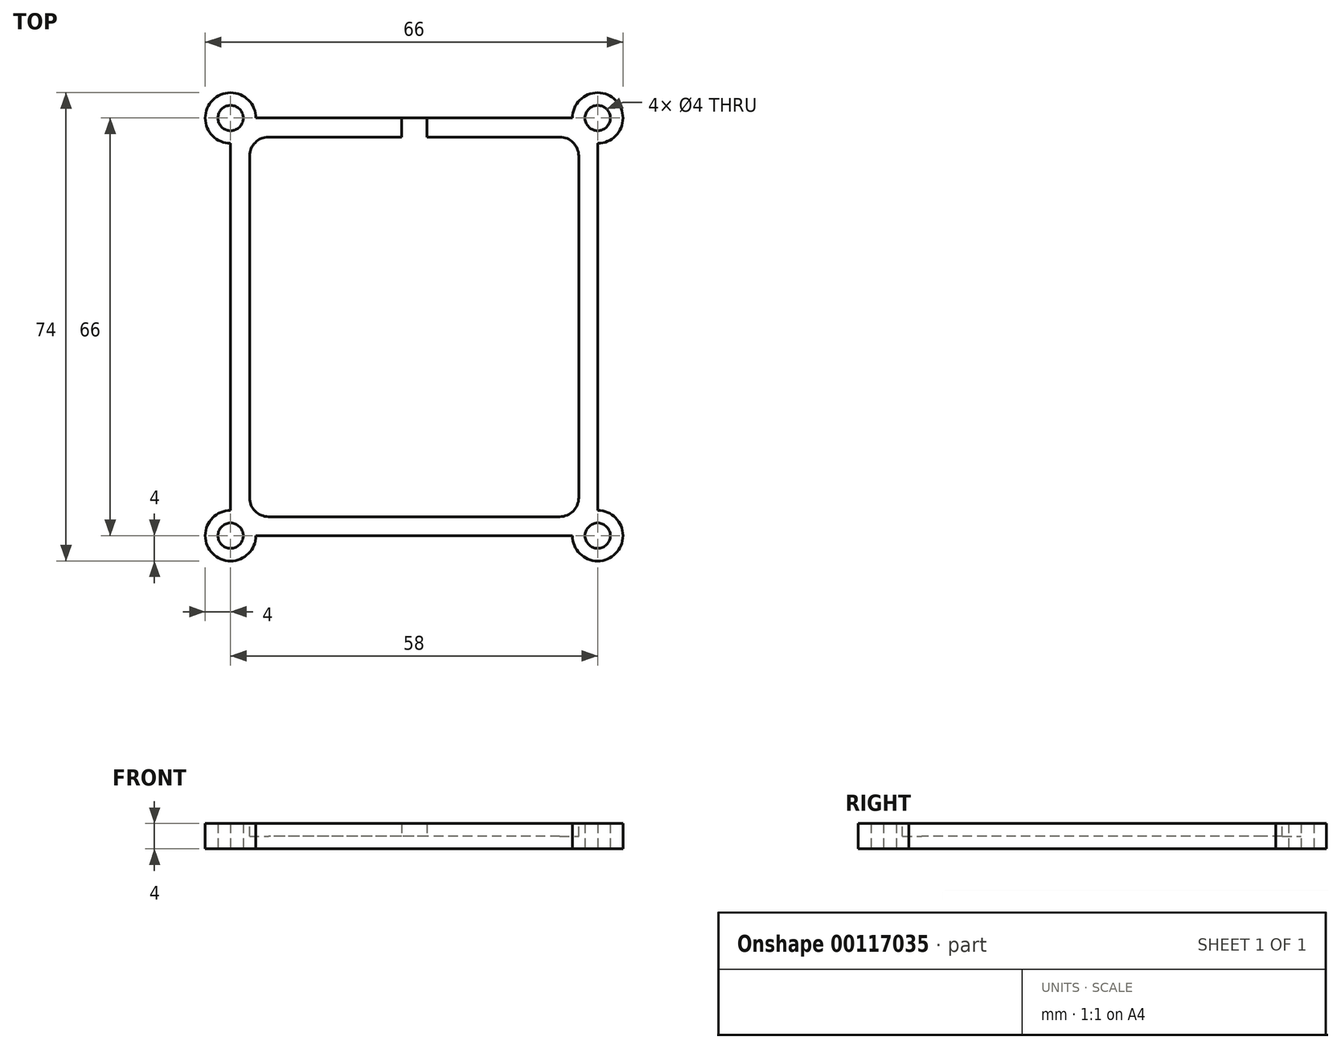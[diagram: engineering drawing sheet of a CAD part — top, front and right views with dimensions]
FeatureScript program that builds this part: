
annotation { "Feature Type Name" : "Feature", "Feature Type Description" : "" }
export const myFeature = defineFeature(function(context is Context, id is Id, definition is map)
    precondition{}
    {
        {
            var Q0;
            Q0=qCreatedBy(makeId("Top.planeOp"),FACE);
            var sketch = newSketch(context, id + "F0", { "sketchPlane" : qUnion([Q0])});
            skLineSegment(sketch, "E0.bottom", {"start": v(25, 29) * mm, "end": v(-25, 29) * mm, "construction": true});
            skLineSegment(sketch, "E0.top", {"start": v(25, -29) * mm, "end": v(-25, -29) * mm, "construction": true});
            skLineSegment(sketch, "E0.left", {"start": v(25, 29) * mm, "end": v(25, -29) * mm, "construction": true});
            skLineSegment(sketch, "E0.right", {"start": v(-25, 29) * mm, "end": v(-25, -29) * mm, "construction": true});
            skPoint(sketch, "E0.middle", {"position": v(0, 0) * mm});
            skLineSegment(sketch, "E1.bottom", {"start": v(-2, 33) * mm, "end": v(2, 33) * mm, "construction": true});
            skLineSegment(sketch, "E1.top", {"start": v(-2, 29) * mm, "end": v(2, 29) * mm, "construction": true});
            skLineSegment(sketch, "E1.left", {"start": v(-2, 33) * mm, "end": v(-2, 29) * mm, "construction": true});
            skLineSegment(sketch, "E1.right", {"start": v(2, 33) * mm, "end": v(2, 29) * mm, "construction": true});
            skPoint(sketch, "E2", {"position": v(0, 33) * mm});
            skSolve(sketch);
        }
        {
            var Q0;
            Q0=qCreatedBy(makeId("Top.planeOp"),FACE);
            var sketch = newSketch(context, id + "F1", { "sketchPlane" : qUnion([Q0])});
            skLineSegment(sketch, "E3.bottom", {"start": v(29, 33) * mm, "end": v(-29, 33) * mm});
            skLineSegment(sketch, "E3.top", {"start": v(29, -33) * mm, "end": v(-29, -33) * mm});
            skLineSegment(sketch, "E3.left", {"start": v(29, 33) * mm, "end": v(29, -33) * mm});
            skLineSegment(sketch, "E3.right", {"start": v(-29, 33) * mm, "end": v(-29, -33) * mm});
            skPoint(sketch, "E3.middle", {"position": v(0, 0) * mm});
            skCircle(sketch, "E4", {"center": v(29, 33) * mm, "radius": 4 * mm});
            skCircle(sketch, "E5.0.1.0", {"center": v(29, -33) * mm, "radius": 4 * mm});
            skCircle(sketch, "E5.1.0.0", {"center": v(-29, 33) * mm, "radius": 4 * mm});
            skCircle(sketch, "E5.1.1.0", {"center": v(-29, -33) * mm, "radius": 4 * mm});
            skLineSegment(sketch, "E5.direction1", {"start": v(29, 33) * mm, "end": v(-29, 33) * mm, "construction": true});
            skLineSegment(sketch, "E5.direction2", {"start": v(29, 33) * mm, "end": v(29, -33) * mm, "construction": true});
            skSolve(sketch);
        }
        {
            var Q0;
            Q0 = qSketchRegion(id + "F1", true);
            extrude(context, id + "F2", {"entities" : qUnion([Q0]), "depth" : 4 * mm});
        }
        {
            var Q0;
            Q0=makeQuery(id+"F2.opExtrude","SWEPT_FACE",FACE,{"disambiguationData":[OSD([sQuery(id+"F1.wireOp",EDGE,"E3.bottom")])]});
            var sketch = newSketch(context, id + "F3", { "sketchPlane" : qUnion([Q0])});
            skLineSegment(sketch, "E6.bottom", {"start": v(-2, 4) * mm, "end": v(2, 4) * mm});
            skLineSegment(sketch, "E6.top", {"start": v(-2, 2) * mm, "end": v(2, 2) * mm});
            skLineSegment(sketch, "E6.left", {"start": v(-2, 4) * mm, "end": v(-2, 2) * mm});
            skLineSegment(sketch, "E6.right", {"start": v(2, 4) * mm, "end": v(2, 2) * mm});
            skPoint(sketch, "E7", {"position": v(0, 4) * mm});
            skSolve(sketch);
        }
        {
            var Q0;
            Q0=makeQuery(id+"F3.imprint","IMPRINT",FACE,{"disambiguationData":[TD([[makeQuery(id+"F3.imprint","IMPRINT",EDGE,{"derivedFrom":sQuery(id+"F3.wireOp",EDGE,"E6.bottom")}),-1.0]])]});
            extrude(context, id + "F4", {"entities" : qUnion([Q0]), "operationType" : NewBodyOperationType.REMOVE, "oppositeDirection" : true, "depth" : 4 * mm});
        }
        {
            var Q0;
            Q0=makeQuery(id+"F2.opExtrude","CAP_FACE",FACE,{"disambiguationData":[OSD([sQuery(id+"F1.wireOp",EDGE,"E3.bottom"),sQuery(id+"F1.wireOp",EDGE,"E3.top"),sQuery(id+"F1.wireOp",EDGE,"E3.left"),sQuery(id+"F1.wireOp",EDGE,"E3.right"),sQuery(id+"F1.wireOp",EDGE,"E4"),sQuery(id+"F1.wireOp",EDGE,"E5.0.1.0"),sQuery(id+"F1.wireOp",EDGE,"E5.1.0.0"),sQuery(id+"F1.wireOp",EDGE,"E5.1.1.0")])],"isStart":false});
            var sketch = newSketch(context, id + "F5", { "sketchPlane" : qUnion([Q0])});
            skLineSegment(sketch, "E8.bottom", {"start": v(26, 30) * mm, "end": v(-26, 30) * mm});
            skLineSegment(sketch, "E8.top", {"start": v(26, -30) * mm, "end": v(-26, -30) * mm});
            skLineSegment(sketch, "E8.left", {"start": v(26, 30) * mm, "end": v(26, -30) * mm});
            skLineSegment(sketch, "E8.right", {"start": v(-26, 30) * mm, "end": v(-26, -30) * mm});
            skPoint(sketch, "E8.middle", {"position": v(0, 0) * mm});
            skSolve(sketch);
        }
        {
            var Q0;
            Q0 = qSketchRegion(id + "F5", true);
            extrude(context, id + "F6", {"entities" : qUnion([Q0]), "operationType" : NewBodyOperationType.REMOVE, "oppositeDirection" : true, "depth" : 2 * mm});
        }
        {
            var Q0;
            Q0=qCreatedBy(makeId("Top.planeOp"),FACE);
            var sketch = newSketch(context, id + "F7", { "sketchPlane" : qUnion([Q0])});
            skCircle(sketch, "E9", {"center": v(29, 33) * mm, "radius": 2 * mm});
            skCircle(sketch, "E10", {"center": v(-29, 33) * mm, "radius": 2 * mm});
            skCircle(sketch, "E11", {"center": v(29, -33) * mm, "radius": 2 * mm});
            skCircle(sketch, "E12", {"center": v(-29, -33) * mm, "radius": 2 * mm});
            skSolve(sketch);
        }
        {
            var Q0;
            Q0 = qSketchRegion(id + "F7", true);
            extrude(context, id + "F8", {"entities" : qUnion([Q0]), "operationType" : NewBodyOperationType.REMOVE, "depth" : 4 * mm});
        }
        {
            var Q0;
            Q0=makeQuery(id+"F6.boolean.opBoolean","COPY",EDGE,{"derivedFrom":makeQuery(id+"F6.opExtrude","SWEPT_EDGE",EDGE,{"disambiguationData":[OSD([sQuery(id+"F5.wireOp",EDGE,"E8.top"),sQuery(id+"F5.wireOp",EDGE,"E8.left")])]})});
            var Q1;
            Q1=makeQuery(id+"F6.boolean.opBoolean","COPY",EDGE,{"derivedFrom":makeQuery(id+"F6.opExtrude","SWEPT_EDGE",EDGE,{"disambiguationData":[OSD([sQuery(id+"F5.wireOp",EDGE,"E8.top"),sQuery(id+"F5.wireOp",EDGE,"E8.right")])]})});
            var Q2;
            Q2=makeQuery(id+"F6.boolean.opBoolean","COPY",EDGE,{"derivedFrom":makeQuery(id+"F6.opExtrude","SWEPT_EDGE",EDGE,{"disambiguationData":[OSD([sQuery(id+"F5.wireOp",EDGE,"E8.bottom"),sQuery(id+"F5.wireOp",EDGE,"E8.right")])]})});
            var Q3;
            Q3=makeQuery(id+"F6.boolean.opBoolean","COPY",EDGE,{"derivedFrom":makeQuery(id+"F6.opExtrude","SWEPT_EDGE",EDGE,{"disambiguationData":[OSD([sQuery(id+"F5.wireOp",EDGE,"E8.bottom"),sQuery(id+"F5.wireOp",EDGE,"E8.left")])]})});
            fillet(context, id + "F9", {"entities" : qUnion([Q0, Q1, Q2, Q3]), "radius" : 3 * mm, "tangentPropagation" : true, "allowEdgeOverflow" : false});
        }
    });
